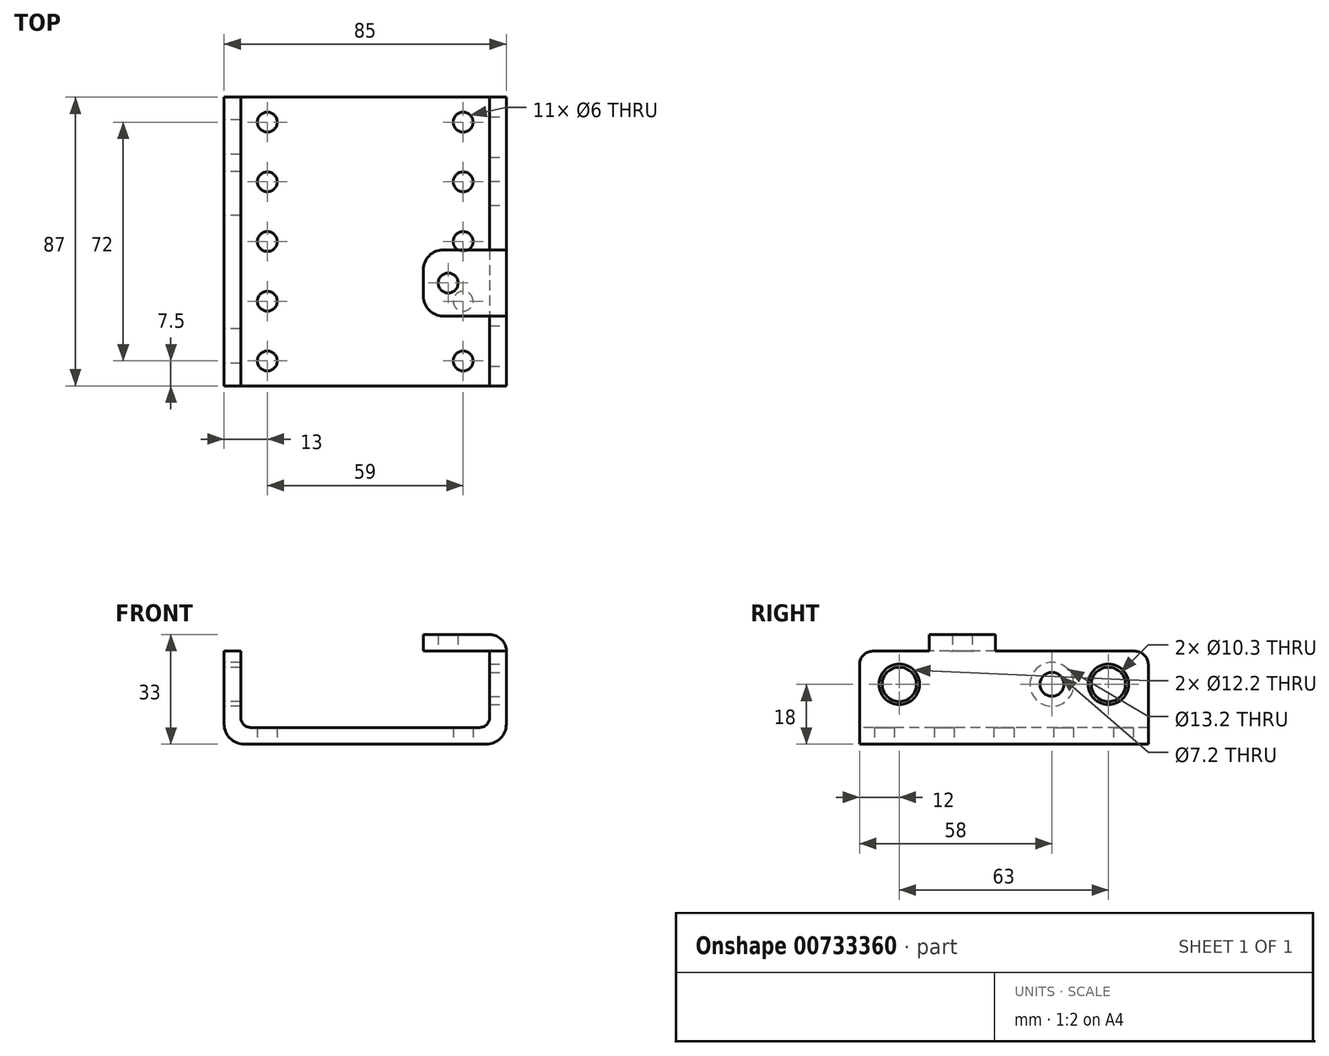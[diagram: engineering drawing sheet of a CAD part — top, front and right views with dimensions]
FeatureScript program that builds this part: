
annotation { "Feature Type Name" : "Feature", "Feature Type Description" : "" }
export const myFeature = defineFeature(function(context is Context, id is Id, definition is map)
    precondition{}
    {
        {
            var Q0;
            Q0=qCreatedBy(makeId("Front.planeOp"),FACE);
            var sketch = newSketch(context, id + "F0", { "sketchPlane" : qUnion([Q0])});
            skLineSegment(sketch, "E0", {"start": v(0, 0) * mm, "end": v(0, 28) * mm});
            skLineSegment(sketch, "E1", {"start": v(0, 28) * mm, "end": v(5, 28) * mm});
            skLineSegment(sketch, "E2", {"start": v(5, 28) * mm, "end": v(5, 5) * mm});
            skLineSegment(sketch, "E3", {"start": v(5, 5) * mm, "end": v(80, 5) * mm});
            skLineSegment(sketch, "E4", {"start": v(80, 5) * mm, "end": v(80, 28) * mm});
            skLineSegment(sketch, "E5", {"start": v(80, 28) * mm, "end": v(85, 28) * mm});
            skLineSegment(sketch, "E6", {"start": v(85, 28) * mm, "end": v(85, 0) * mm});
            skLineSegment(sketch, "E7", {"start": v(85, 0) * mm, "end": v(0, 0) * mm});
            skSolve(sketch);
        }
        {
            var Q0;
            Q0=qSketchRegion(id+"F0",true);
            extrude(context, id + "F1", {"entities" : qUnion([Q0]), "oppositeDirection" : true, "depth" : 87 * mm, "offsetDistance" : 25 * mm});
        }
        {
            var Q0;
            Q0=makeQuery(id+"F1.opExtrude","SWEPT_EDGE",EDGE,{"disambiguationData":[OSD([sQuery(id+"F0.wireOp",EDGE,"E2"),sQuery(id+"F0.wireOp",EDGE,"E3")])]});
            fillet(context, id + "F2", {"entities" : qUnion([Q0]), "radius" : 3 * mm, "tangentPropagation" : true, "allowEdgeOverflow" : false});
        }
        {
            var Q0;
            Q0=makeQuery(id+"F1.opExtrude","SWEPT_EDGE",EDGE,{"disambiguationData":[OSD([sQuery(id+"F0.wireOp",EDGE,"E0"),sQuery(id+"F0.wireOp",EDGE,"E7")])]});
            var Q1;
            Q1=makeQuery(id+"F1.opExtrude","SWEPT_EDGE",EDGE,{"disambiguationData":[OSD([sQuery(id+"F0.wireOp",EDGE,"E6"),sQuery(id+"F0.wireOp",EDGE,"E7")])]});
            fillet(context, id + "F3", {"entities" : qUnion([Q0, Q1]), "radius" : 6 * mm, "tangentPropagation" : true, "allowEdgeOverflow" : false});
        }
        {
            var Q0;
            Q0=makeQuery(id+"F1.opExtrude","SWEPT_EDGE",EDGE,{"disambiguationData":[OSD([sQuery(id+"F0.wireOp",EDGE,"E3"),sQuery(id+"F0.wireOp",EDGE,"E4")])]});
            fillet(context, id + "F4", {"entities" : qUnion([Q0]), "radius" : 3 * mm, "tangentPropagation" : true, "allowEdgeOverflow" : false});
        }
        {
            var Q0;
            Q0=makeQuery(id+"F1.opExtrude","CAP_EDGE",EDGE,{"disambiguationData":[OSD([sQuery(id+"F0.wireOp",EDGE,"E5")])],"isStart":true});
            var Q1;
            Q1=makeQuery(id+"F1.opExtrude","CAP_EDGE",EDGE,{"disambiguationData":[OSD([sQuery(id+"F0.wireOp",EDGE,"E1")])],"isStart":true});
            var Q2;
            Q2=makeQuery(id+"F1.opExtrude","CAP_EDGE",EDGE,{"disambiguationData":[OSD([sQuery(id+"F0.wireOp",EDGE,"E1")])],"isStart":false});
            var Q3;
            Q3=makeQuery(id+"F1.opExtrude","CAP_EDGE",EDGE,{"disambiguationData":[OSD([sQuery(id+"F0.wireOp",EDGE,"E5")])],"isStart":false});
            fillet(context, id + "F5", {"entities" : qUnion([Q0, Q1, Q2, Q3]), "radius" : 4 * mm, "tangentPropagation" : true, "allowEdgeOverflow" : false});
        }
        {
            var Q0;
            Q0=makeQuery(id+"F1.opExtrude","SWEPT_FACE",FACE,{"disambiguationData":[OSD([sQuery(id+"F0.wireOp",EDGE,"E5")])]});
            var sketch = newSketch(context, id + "F6", { "sketchPlane" : qUnion([Q0])});
            skLineSegment(sketch, "E8", {"start": v(85, 21) * mm, "end": v(60, 21) * mm});
            skLineSegment(sketch, "E9", {"start": v(60, 21) * mm, "end": v(60, 41) * mm});
            skLineSegment(sketch, "E10", {"start": v(60, 41) * mm, "end": v(85, 41) * mm});
            skLineSegment(sketch, "E11", {"start": v(85, 41) * mm, "end": v(85, 21) * mm});
            skCircle(sketch, "E12", {"center": v(67.5, 31) * mm, "radius": 3 * mm});
            skSolve(sketch);
        }
        {
            var Q0;
            Q0=qSketchRegion(id+"F6",true);
            extrude(context, id + "F7", {"entities" : qUnion([Q0]), "operationType" : NewBodyOperationType.ADD, "depth" : 5 * mm, "offsetDistance" : 25 * mm});
        }
        {
            var Q0;
            Q0=makeQuery(id+"F7.opExtrude","CAP_EDGE",EDGE,{"disambiguationData":[OSD([sQuery(id+"F6.wireOp",EDGE,"E11")])],"isStart":false});
            fillet(context, id + "F8", {"entities" : qUnion([Q0]), "radius" : 5 * mm, "tangentPropagation" : true, "allowEdgeOverflow" : false});
        }
        {
            var Q0;
            Q0=makeQuery(id+"F7.opExtrude","SWEPT_EDGE",EDGE,{"disambiguationData":[OSD([sQuery(id+"F6.wireOp",EDGE,"E8"),sQuery(id+"F6.wireOp",EDGE,"E9")])]});
            var Q1;
            Q1=makeQuery(id+"F7.opExtrude","SWEPT_EDGE",EDGE,{"disambiguationData":[OSD([sQuery(id+"F6.wireOp",EDGE,"E9"),sQuery(id+"F6.wireOp",EDGE,"E10")])]});
            fillet(context, id + "F9", {"entities" : qUnion([Q0, Q1]), "radius" : 6 * mm, "tangentPropagation" : true, "allowEdgeOverflow" : false});
        }
        {
            var Q0;
            Q0=makeQuery(id+"F1.opExtrude","SWEPT_FACE",FACE,{"disambiguationData":[OSD([sQuery(id+"F0.wireOp",EDGE,"E0")])]});
            var sketch = newSketch(context, id + "F10", { "sketchPlane" : qUnion([Q0])});
            skCircle(sketch, "E13", {"center": v(-12, 18) * mm, "radius": 5.15 * mm});
            skCircle(sketch, "E14", {"center": v(-58, 18) * mm, "radius": 6.6 * mm});
            skCircle(sketch, "E15", {"center": v(-75, 18) * mm, "radius": 5.15 * mm});
            skSolve(sketch);
        }
        {
            var Q0;
            Q0=qSketchRegion(id+"F10",true);
            extrude(context, id + "F11", {"entities" : qUnion([Q0]), "operationType" : NewBodyOperationType.REMOVE, "oppositeDirection" : true, "depth" : 25 * mm, "offsetDistance" : 25 * mm});
        }
        {
            var Q0;
            Q0=makeQuery(id+"F7.boolean.opBoolean","MERGE",FACE,{"derivedFrom":[makeQuery(id+"F1.opExtrude","SWEPT_FACE",FACE,{"disambiguationData":[OSD([sQuery(id+"F0.wireOp",EDGE,"E6")])]}),makeQuery(id+"F7.opExtrude","SWEPT_FACE",FACE,{"disambiguationData":[OSD([sQuery(id+"F6.wireOp",EDGE,"E11")])]})]});
            var sketch = newSketch(context, id + "F12", { "sketchPlane" : qUnion([Q0])});
            skCircle(sketch, "E16", {"center": v(75, 18) * mm, "radius": 6.1 * mm});
            skCircle(sketch, "E17", {"center": v(58, 18) * mm, "radius": 3.6 * mm});
            skCircle(sketch, "E18", {"center": v(12, 18) * mm, "radius": 6.1 * mm});
            skSolve(sketch);
        }
        {
            var Q0;
            Q0=qSketchRegion(id+"F12",true);
            extrude(context, id + "F13", {"entities" : qUnion([Q0]), "operationType" : NewBodyOperationType.REMOVE, "oppositeDirection" : true, "depth" : 25 * mm, "offsetDistance" : 25 * mm});
        }
        {
            var Q0;
            Q0=makeQuery(id+"F1.opExtrude","SWEPT_FACE",FACE,{"disambiguationData":[OSD([sQuery(id+"F0.wireOp",EDGE,"E7")])]});
            var sketch = newSketch(context, id + "F14", { "sketchPlane" : qUnion([Q0])});
            skCircle(sketch, "E19", {"center": v(13, -7.5) * mm, "radius": 3 * mm});
            skCircle(sketch, "E20", {"center": v(13, -25.5) * mm, "radius": 3 * mm});
            skCircle(sketch, "E21", {"center": v(13, -43.5) * mm, "radius": 3 * mm});
            skCircle(sketch, "E22", {"center": v(13, -79.5) * mm, "radius": 3 * mm});
            skCircle(sketch, "E23", {"center": v(13, -61.5) * mm, "radius": 3 * mm});
            skCircle(sketch, "E24.MirrorC", {"center": v(72, -79.5) * mm, "radius": 3 * mm});
            skCircle(sketch, "E25.MirrorC", {"center": v(72, -61.5) * mm, "radius": 3 * mm});
            skCircle(sketch, "E26.MirrorC", {"center": v(72, -43.5) * mm, "radius": 3 * mm});
            skCircle(sketch, "E27.MirrorC", {"center": v(72, -7.5) * mm, "radius": 3 * mm});
            skCircle(sketch, "E28.MirrorC", {"center": v(72, -25.5) * mm, "radius": 3 * mm});
            skSolve(sketch);
        }
        {
            var Q0;
            Q0=qSketchRegion(id+"F14",true);
            extrude(context, id + "F15", {"entities" : qUnion([Q0]), "operationType" : NewBodyOperationType.REMOVE, "oppositeDirection" : true, "depth" : 25 * mm, "offsetDistance" : 25 * mm});
        }
    });
